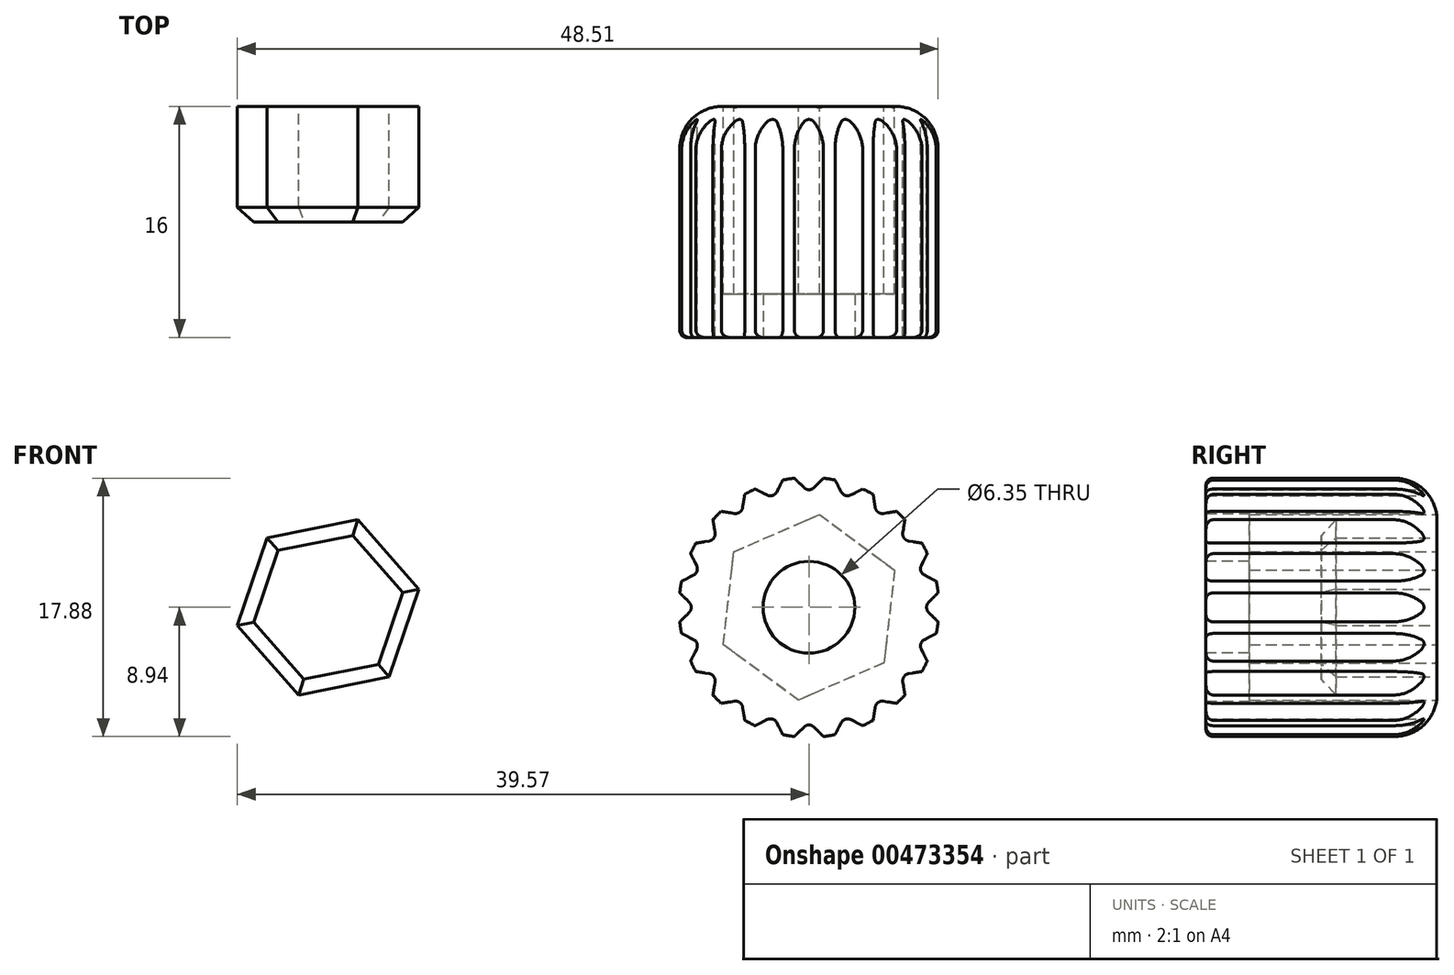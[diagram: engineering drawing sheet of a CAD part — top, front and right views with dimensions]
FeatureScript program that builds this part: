
annotation { "Feature Type Name" : "Feature", "Feature Type Description" : "" }
export const myFeature = defineFeature(function(context is Context, id is Id, definition is map)
    precondition{}
    {
        {
            var Q0;
            Q0=qCreatedBy(makeId("Front.planeOp"),FACE);
            var sketch = newSketch(context, id + "F0", { "sketchPlane" : qUnion([Q0])});
            skCircle(sketch, "E0", {"center": v(0, 0) * mm, "radius": 9 * mm});
            skSolve(sketch);
        }
        {
            var Q0;
            Q0=makeQuery(id+"F0.imprint","IMPRINT",FACE,{"disambiguationData":[TD([[makeQuery(id+"F0.imprint","IMPRINT",EDGE,{"derivedFrom":sQuery(id+"F0.wireOp",EDGE,"E0")}),1.0]])]});
            extrude(context, id + "F1", {"entities" : qUnion([Q0]), "depth" : 16 * mm});
        }
        {
            var Q0;
            Q0=makeQuery(id+"F1.opExtrude","CAP_EDGE",EDGE,{"disambiguationData":[OSD([sQuery(id+"F0.wireOp",EDGE,"E0")])],"isStart":true});
            fillet(context, id + "F2", {"entities" : qUnion([Q0]), "radius" : 3 * mm, "tangentPropagation" : true, "allowEdgeOverflow" : false});
        }
        {
            var Q0;
            Q0=qCreatedBy(makeId("Front.planeOp"),FACE);
            var sketch = newSketch(context, id + "F3", { "sketchPlane" : qUnion([Q0])});
            skLineSegment(sketch, "E1.bottom", {"start": v(10.06, 0) * mm, "end": v(9, 1.06) * mm});
            skLineSegment(sketch, "E1.top", {"start": v(9, -1.06) * mm, "end": v(7.94, 0) * mm});
            skLineSegment(sketch, "E1.left", {"start": v(10.06, 0) * mm, "end": v(9, -1.06) * mm});
            skLineSegment(sketch, "E1.right", {"start": v(9, 1.06) * mm, "end": v(7.94, 0) * mm});
            skPoint(sketch, "E1.middle", {"position": v(9, 0) * mm});
            skSolve(sketch);
        }
        {
            var Q0;
            Q0=makeQuery(id+"F3.imprint","IMPRINT",FACE,{"disambiguationData":[TD([[makeQuery(id+"F3.imprint","IMPRINT",EDGE,{"derivedFrom":sQuery(id+"F3.wireOp",EDGE,"E1.bottom")}),1.0]])]});
            extrude(context, id + "F4", {"entities" : qUnion([Q0]), "depth" : 25 * mm});
        }
        {
            var Q0;
            Q0=makeQuery(id+"F4.opExtrude","SWEPT_BODY",BODY,{"disambiguationData":[OSD([sQuery(id+"F3.wireOp",EDGE,"E1.bottom"),sQuery(id+"F3.wireOp",EDGE,"E1.top"),sQuery(id+"F3.wireOp",EDGE,"E1.left"),sQuery(id+"F3.wireOp",EDGE,"E1.right")])]});
            var Q1;
            Q1=sQuery(id+"F0.wireOp",EDGE,"E0");
            circularPattern(context, id + "F5", {"operationType" : NewBodyOperationType.REMOVE, "entities" : qUnion([Q0]), "axis" : qUnion([Q1]), "angle" : 360 * degree, "instanceCount" : 20, "equalSpace" : true});
        }
        {
            var Q0;
            Q0=qCreatedBy(makeId("Front.planeOp"),FACE);
            var sketch = newSketch(context, id + "F6", { "sketchPlane" : qUnion([Q0])});
            skCircle(sketch, "E2.cCircle", {"center": v(0, 0) * mm, "radius": 6.47 * mm, "construction": true});
            skLineSegment(sketch, "E2.0", {"start": v(5.2, -3.84) * mm, "end": v(-0.73, -6.42) * mm});
            skLineSegment(sketch, "E2.1", {"start": v(-0.73, -6.42) * mm, "end": v(-5.93, -2.58) * mm});
            skLineSegment(sketch, "E2.2", {"start": v(-5.93, -2.58) * mm, "end": v(-5.2, 3.84) * mm});
            skLineSegment(sketch, "E2.3", {"start": v(-5.2, 3.84) * mm, "end": v(0.73, 6.42) * mm});
            skLineSegment(sketch, "E2.4", {"start": v(0.73, 6.42) * mm, "end": v(5.93, 2.58) * mm});
            skLineSegment(sketch, "E2.5", {"start": v(5.93, 2.58) * mm, "end": v(5.2, -3.84) * mm});
            skSolve(sketch);
        }
        {
            var Q0;
            Q0 = qSketchRegion(id + "F6", true);
            extrude(context, id + "F7", {"entities" : qUnion([Q0]), "operationType" : NewBodyOperationType.REMOVE, "depth" : 13 * mm});
        }
        {
            var Q0;
            Q0=qCreatedBy(makeId("Front.planeOp"),FACE);
            var sketch = newSketch(context, id + "F8", { "sketchPlane" : qUnion([Q0])});
            skCircle(sketch, "E3", {"center": v(0, 0) * mm, "radius": 3.17 * mm});
            skSolve(sketch);
        }
        {
            var Q0;
            Q0 = qSketchRegion(id + "F8", true);
            extrude(context, id + "F9", {"entities" : qUnion([Q0]), "operationType" : NewBodyOperationType.REMOVE, "endBound" : BoundingType.SYMMETRIC, "oppositeDirection" : true, "depth" : 40 * mm});
        }
        {
            var Q0;
            Q0=qCreatedBy(makeId("Front.planeOp"),FACE);
            var sketch = newSketch(context, id + "F10", { "sketchPlane" : qUnion([Q0])});
            skCircle(sketch, "E4.cCircle", {"center": v(-33.28, 0) * mm, "radius": 5.55 * mm, "construction": true});
            skLineSegment(sketch, "E4.0", {"start": v(-35.34, -6.07) * mm, "end": v(-39.57, -1.25) * mm});
            skLineSegment(sketch, "E4.1", {"start": v(-39.57, -1.25) * mm, "end": v(-37.5, 4.82) * mm});
            skLineSegment(sketch, "E4.2", {"start": v(-37.5, 4.82) * mm, "end": v(-31.22, 6.07) * mm});
            skLineSegment(sketch, "E4.3", {"start": v(-31.22, 6.07) * mm, "end": v(-27, 1.25) * mm});
            skLineSegment(sketch, "E4.4", {"start": v(-27, 1.25) * mm, "end": v(-29.06, -4.82) * mm});
            skLineSegment(sketch, "E4.5", {"start": v(-29.06, -4.82) * mm, "end": v(-35.34, -6.07) * mm});
            skPoint(sketch, "E4.0.midPoint", {"position": v(-37.45, -3.66) * mm});
            skSolve(sketch);
        }
        {
            var Q0;
            Q0=makeQuery(id+"F10.imprint","IMPRINT",FACE,{"disambiguationData":[TD([[makeQuery(id+"F10.imprint","IMPRINT",EDGE,{"derivedFrom":sQuery(id+"F10.wireOp",EDGE,"E4.0")}),-1.0]])]});
            extrude(context, id + "F11", {"entities" : qUnion([Q0]), "depth" : 8 * mm});
        }
        {
            var Q0;
            Q0=makeQuery(id+"F5.boolean.opBoolean","INTERSECT",EDGE,{"derivedFrom":[makeQuery(id+"F5.opPattern","COPY",FACE,{"derivedFrom":makeQuery(id+"F4.opExtrude","SWEPT_FACE",FACE,{"disambiguationData":[OSD([sQuery(id+"F3.wireOp",EDGE,"E1.right")])]}),"instanceName":"11"}),makeQuery(id+"F5.opPattern","COPY",FACE,{"derivedFrom":makeQuery(id+"F4.opExtrude","SWEPT_FACE",FACE,{"disambiguationData":[OSD([sQuery(id+"F3.wireOp",EDGE,"E1.top")])]}),"instanceName":"12"})]});
            var Q1;
            Q1=makeQuery(id+"F5.boolean.opBoolean","INTERSECT",EDGE,{"derivedFrom":[makeQuery(id+"F5.opPattern","COPY",FACE,{"derivedFrom":makeQuery(id+"F4.opExtrude","SWEPT_FACE",FACE,{"disambiguationData":[OSD([sQuery(id+"F3.wireOp",EDGE,"E1.right")])]}),"instanceName":"10"}),makeQuery(id+"F5.opPattern","COPY",FACE,{"derivedFrom":makeQuery(id+"F4.opExtrude","SWEPT_FACE",FACE,{"disambiguationData":[OSD([sQuery(id+"F3.wireOp",EDGE,"E1.top")])]}),"instanceName":"11"})]});
            var Q2;
            Q2=makeQuery(id+"F5.boolean.opBoolean","INTERSECT",EDGE,{"derivedFrom":[makeQuery(id+"F5.opPattern","COPY",FACE,{"derivedFrom":makeQuery(id+"F4.opExtrude","SWEPT_FACE",FACE,{"disambiguationData":[OSD([sQuery(id+"F3.wireOp",EDGE,"E1.right")])]}),"instanceName":"9"}),makeQuery(id+"F5.opPattern","COPY",FACE,{"derivedFrom":makeQuery(id+"F4.opExtrude","SWEPT_FACE",FACE,{"disambiguationData":[OSD([sQuery(id+"F3.wireOp",EDGE,"E1.top")])]}),"instanceName":"10"})]});
            var Q3;
            Q3=makeQuery(id+"F5.boolean.opBoolean","INTERSECT",EDGE,{"derivedFrom":[makeQuery(id+"F5.opPattern","COPY",FACE,{"derivedFrom":makeQuery(id+"F4.opExtrude","SWEPT_FACE",FACE,{"disambiguationData":[OSD([sQuery(id+"F3.wireOp",EDGE,"E1.right")])]}),"instanceName":"8"}),makeQuery(id+"F5.opPattern","COPY",FACE,{"derivedFrom":makeQuery(id+"F4.opExtrude","SWEPT_FACE",FACE,{"disambiguationData":[OSD([sQuery(id+"F3.wireOp",EDGE,"E1.top")])]}),"instanceName":"9"})]});
            var Q4;
            Q4=makeQuery(id+"F5.boolean.opBoolean","INTERSECT",EDGE,{"derivedFrom":[makeQuery(id+"F5.opPattern","COPY",FACE,{"derivedFrom":makeQuery(id+"F4.opExtrude","SWEPT_FACE",FACE,{"disambiguationData":[OSD([sQuery(id+"F3.wireOp",EDGE,"E1.right")])]}),"instanceName":"7"}),makeQuery(id+"F5.opPattern","COPY",FACE,{"derivedFrom":makeQuery(id+"F4.opExtrude","SWEPT_FACE",FACE,{"disambiguationData":[OSD([sQuery(id+"F3.wireOp",EDGE,"E1.top")])]}),"instanceName":"8"})]});
            var Q5;
            Q5=makeQuery(id+"F5.boolean.opBoolean","INTERSECT",EDGE,{"derivedFrom":[makeQuery(id+"F5.opPattern","COPY",FACE,{"derivedFrom":makeQuery(id+"F4.opExtrude","SWEPT_FACE",FACE,{"disambiguationData":[OSD([sQuery(id+"F3.wireOp",EDGE,"E1.right")])]}),"instanceName":"6"}),makeQuery(id+"F5.opPattern","COPY",FACE,{"derivedFrom":makeQuery(id+"F4.opExtrude","SWEPT_FACE",FACE,{"disambiguationData":[OSD([sQuery(id+"F3.wireOp",EDGE,"E1.top")])]}),"instanceName":"7"})]});
            var Q6;
            Q6=makeQuery(id+"F5.boolean.opBoolean","INTERSECT",EDGE,{"derivedFrom":[makeQuery(id+"F5.opPattern","COPY",FACE,{"derivedFrom":makeQuery(id+"F4.opExtrude","SWEPT_FACE",FACE,{"disambiguationData":[OSD([sQuery(id+"F3.wireOp",EDGE,"E1.right")])]}),"instanceName":"5"}),makeQuery(id+"F5.opPattern","COPY",FACE,{"derivedFrom":makeQuery(id+"F4.opExtrude","SWEPT_FACE",FACE,{"disambiguationData":[OSD([sQuery(id+"F3.wireOp",EDGE,"E1.top")])]}),"instanceName":"6"})]});
            var Q7;
            Q7=makeQuery(id+"F5.boolean.opBoolean","INTERSECT",EDGE,{"derivedFrom":[makeQuery(id+"F5.opPattern","COPY",FACE,{"derivedFrom":makeQuery(id+"F4.opExtrude","SWEPT_FACE",FACE,{"disambiguationData":[OSD([sQuery(id+"F3.wireOp",EDGE,"E1.right")])]}),"instanceName":"4"}),makeQuery(id+"F5.opPattern","COPY",FACE,{"derivedFrom":makeQuery(id+"F4.opExtrude","SWEPT_FACE",FACE,{"disambiguationData":[OSD([sQuery(id+"F3.wireOp",EDGE,"E1.top")])]}),"instanceName":"5"})]});
            var Q8;
            Q8=makeQuery(id+"F5.boolean.opBoolean","INTERSECT",EDGE,{"derivedFrom":[makeQuery(id+"F5.opPattern","COPY",FACE,{"derivedFrom":makeQuery(id+"F4.opExtrude","SWEPT_FACE",FACE,{"disambiguationData":[OSD([sQuery(id+"F3.wireOp",EDGE,"E1.right")])]}),"instanceName":"3"}),makeQuery(id+"F5.opPattern","COPY",FACE,{"derivedFrom":makeQuery(id+"F4.opExtrude","SWEPT_FACE",FACE,{"disambiguationData":[OSD([sQuery(id+"F3.wireOp",EDGE,"E1.top")])]}),"instanceName":"4"})]});
            var Q9;
            Q9=makeQuery(id+"F5.boolean.opBoolean","INTERSECT",EDGE,{"derivedFrom":[makeQuery(id+"F5.opPattern","COPY",FACE,{"derivedFrom":makeQuery(id+"F4.opExtrude","SWEPT_FACE",FACE,{"disambiguationData":[OSD([sQuery(id+"F3.wireOp",EDGE,"E1.right")])]}),"instanceName":"2"}),makeQuery(id+"F5.opPattern","COPY",FACE,{"derivedFrom":makeQuery(id+"F4.opExtrude","SWEPT_FACE",FACE,{"disambiguationData":[OSD([sQuery(id+"F3.wireOp",EDGE,"E1.top")])]}),"instanceName":"3"})]});
            var Q10;
            Q10=makeQuery(id+"F5.boolean.opBoolean","INTERSECT",EDGE,{"derivedFrom":[makeQuery(id+"F5.opPattern","COPY",FACE,{"derivedFrom":makeQuery(id+"F4.opExtrude","SWEPT_FACE",FACE,{"disambiguationData":[OSD([sQuery(id+"F3.wireOp",EDGE,"E1.right")])]}),"instanceName":"1"}),makeQuery(id+"F5.opPattern","COPY",FACE,{"derivedFrom":makeQuery(id+"F4.opExtrude","SWEPT_FACE",FACE,{"disambiguationData":[OSD([sQuery(id+"F3.wireOp",EDGE,"E1.top")])]}),"instanceName":"2"})]});
            var Q11;
            Q11=makeQuery(id+"F5.boolean.opBoolean","INTERSECT",EDGE,{"derivedFrom":[makeQuery(id+"F4.opExtrude","SWEPT_FACE",FACE,{"disambiguationData":[OSD([sQuery(id+"F3.wireOp",EDGE,"E1.right")])]}),makeQuery(id+"F5.opPattern","COPY",FACE,{"derivedFrom":makeQuery(id+"F4.opExtrude","SWEPT_FACE",FACE,{"disambiguationData":[OSD([sQuery(id+"F3.wireOp",EDGE,"E1.top")])]}),"instanceName":"1"})]});
            var Q12;
            Q12=makeQuery(id+"F5.boolean.opBoolean","COPY",EDGE,{"derivedFrom":makeQuery(id+"F5.opPattern","COPY",EDGE,{"derivedFrom":makeQuery(id+"F4.opExtrude","SWEPT_EDGE",EDGE,{"disambiguationData":[OSD([sQuery(id+"F3.wireOp",EDGE,"E1.top"),sQuery(id+"F3.wireOp",EDGE,"E1.right")])]}),"instanceName":"1"})});
            var Q13;
            Q13=makeQuery(id+"F5.boolean.opBoolean","COPY",EDGE,{"derivedFrom":makeQuery(id+"F5.opPattern","COPY",EDGE,{"derivedFrom":makeQuery(id+"F4.opExtrude","SWEPT_EDGE",EDGE,{"disambiguationData":[OSD([sQuery(id+"F3.wireOp",EDGE,"E1.top"),sQuery(id+"F3.wireOp",EDGE,"E1.right")])]}),"instanceName":"2"})});
            var Q14;
            Q14=makeQuery(id+"F5.boolean.opBoolean","COPY",EDGE,{"derivedFrom":makeQuery(id+"F5.opPattern","COPY",EDGE,{"derivedFrom":makeQuery(id+"F4.opExtrude","SWEPT_EDGE",EDGE,{"disambiguationData":[OSD([sQuery(id+"F3.wireOp",EDGE,"E1.top"),sQuery(id+"F3.wireOp",EDGE,"E1.right")])]}),"instanceName":"3"})});
            var Q15;
            Q15=makeQuery(id+"F5.boolean.opBoolean","COPY",EDGE,{"derivedFrom":makeQuery(id+"F5.opPattern","COPY",EDGE,{"derivedFrom":makeQuery(id+"F4.opExtrude","SWEPT_EDGE",EDGE,{"disambiguationData":[OSD([sQuery(id+"F3.wireOp",EDGE,"E1.top"),sQuery(id+"F3.wireOp",EDGE,"E1.right")])]}),"instanceName":"4"})});
            var Q16;
            Q16=makeQuery(id+"F5.boolean.opBoolean","COPY",EDGE,{"derivedFrom":makeQuery(id+"F4.opExtrude","SWEPT_EDGE",EDGE,{"disambiguationData":[OSD([sQuery(id+"F3.wireOp",EDGE,"E1.top"),sQuery(id+"F3.wireOp",EDGE,"E1.right")])]})});
            var Q17;
            Q17=makeQuery(id+"F5.boolean.opBoolean","COPY",EDGE,{"derivedFrom":makeQuery(id+"F5.opPattern","COPY",EDGE,{"derivedFrom":makeQuery(id+"F4.opExtrude","SWEPT_EDGE",EDGE,{"disambiguationData":[OSD([sQuery(id+"F3.wireOp",EDGE,"E1.top"),sQuery(id+"F3.wireOp",EDGE,"E1.right")])]}),"instanceName":"29"})});
            var Q18;
            Q18=makeQuery(id+"F5.boolean.opBoolean","INTERSECT",EDGE,{"derivedFrom":[makeQuery(id+"F4.opExtrude","SWEPT_FACE",FACE,{"disambiguationData":[OSD([sQuery(id+"F3.wireOp",EDGE,"E1.top")])]}),makeQuery(id+"F5.opPattern","COPY",FACE,{"derivedFrom":makeQuery(id+"F4.opExtrude","SWEPT_FACE",FACE,{"disambiguationData":[OSD([sQuery(id+"F3.wireOp",EDGE,"E1.right")])]}),"instanceName":"29"})]});
            var Q19;
            Q19=makeQuery(id+"F5.boolean.opBoolean","INTERSECT",EDGE,{"derivedFrom":[makeQuery(id+"F5.opPattern","COPY",FACE,{"derivedFrom":makeQuery(id+"F4.opExtrude","SWEPT_FACE",FACE,{"disambiguationData":[OSD([sQuery(id+"F3.wireOp",EDGE,"E1.right")])]}),"instanceName":"28"}),makeQuery(id+"F5.opPattern","COPY",FACE,{"derivedFrom":makeQuery(id+"F4.opExtrude","SWEPT_FACE",FACE,{"disambiguationData":[OSD([sQuery(id+"F3.wireOp",EDGE,"E1.top")])]}),"instanceName":"29"})]});
            var Q20;
            Q20=makeQuery(id+"F5.boolean.opBoolean","INTERSECT",EDGE,{"derivedFrom":[makeQuery(id+"F5.opPattern","COPY",FACE,{"derivedFrom":makeQuery(id+"F4.opExtrude","SWEPT_FACE",FACE,{"disambiguationData":[OSD([sQuery(id+"F3.wireOp",EDGE,"E1.right")])]}),"instanceName":"27"}),makeQuery(id+"F5.opPattern","COPY",FACE,{"derivedFrom":makeQuery(id+"F4.opExtrude","SWEPT_FACE",FACE,{"disambiguationData":[OSD([sQuery(id+"F3.wireOp",EDGE,"E1.top")])]}),"instanceName":"28"})]});
            var Q21;
            Q21=makeQuery(id+"F5.boolean.opBoolean","INTERSECT",EDGE,{"derivedFrom":[makeQuery(id+"F5.opPattern","COPY",FACE,{"derivedFrom":makeQuery(id+"F4.opExtrude","SWEPT_FACE",FACE,{"disambiguationData":[OSD([sQuery(id+"F3.wireOp",EDGE,"E1.right")])]}),"instanceName":"26"}),makeQuery(id+"F5.opPattern","COPY",FACE,{"derivedFrom":makeQuery(id+"F4.opExtrude","SWEPT_FACE",FACE,{"disambiguationData":[OSD([sQuery(id+"F3.wireOp",EDGE,"E1.top")])]}),"instanceName":"27"})]});
            var Q22;
            Q22=makeQuery(id+"F5.boolean.opBoolean","COPY",EDGE,{"derivedFrom":makeQuery(id+"F5.opPattern","COPY",EDGE,{"derivedFrom":makeQuery(id+"F4.opExtrude","SWEPT_EDGE",EDGE,{"disambiguationData":[OSD([sQuery(id+"F3.wireOp",EDGE,"E1.top"),sQuery(id+"F3.wireOp",EDGE,"E1.right")])]}),"instanceName":"28"})});
            var Q23;
            Q23=makeQuery(id+"F5.boolean.opBoolean","COPY",EDGE,{"derivedFrom":makeQuery(id+"F5.opPattern","COPY",EDGE,{"derivedFrom":makeQuery(id+"F4.opExtrude","SWEPT_EDGE",EDGE,{"disambiguationData":[OSD([sQuery(id+"F3.wireOp",EDGE,"E1.top"),sQuery(id+"F3.wireOp",EDGE,"E1.right")])]}),"instanceName":"27"})});
            var Q24;
            Q24=makeQuery(id+"F5.boolean.opBoolean","COPY",EDGE,{"derivedFrom":makeQuery(id+"F5.opPattern","COPY",EDGE,{"derivedFrom":makeQuery(id+"F4.opExtrude","SWEPT_EDGE",EDGE,{"disambiguationData":[OSD([sQuery(id+"F3.wireOp",EDGE,"E1.top"),sQuery(id+"F3.wireOp",EDGE,"E1.right")])]}),"instanceName":"26"})});
            var Q25;
            Q25=makeQuery(id+"F5.boolean.opBoolean","INTERSECT",EDGE,{"derivedFrom":[makeQuery(id+"F5.opPattern","COPY",FACE,{"derivedFrom":makeQuery(id+"F4.opExtrude","SWEPT_FACE",FACE,{"disambiguationData":[OSD([sQuery(id+"F3.wireOp",EDGE,"E1.right")])]}),"instanceName":"25"}),makeQuery(id+"F5.opPattern","COPY",FACE,{"derivedFrom":makeQuery(id+"F4.opExtrude","SWEPT_FACE",FACE,{"disambiguationData":[OSD([sQuery(id+"F3.wireOp",EDGE,"E1.top")])]}),"instanceName":"26"})]});
            var Q26;
            Q26=makeQuery(id+"F5.boolean.opBoolean","COPY",EDGE,{"derivedFrom":makeQuery(id+"F5.opPattern","COPY",EDGE,{"derivedFrom":makeQuery(id+"F4.opExtrude","SWEPT_EDGE",EDGE,{"disambiguationData":[OSD([sQuery(id+"F3.wireOp",EDGE,"E1.top"),sQuery(id+"F3.wireOp",EDGE,"E1.right")])]}),"instanceName":"24"})});
            var Q27;
            Q27=makeQuery(id+"F5.boolean.opBoolean","COPY",EDGE,{"derivedFrom":makeQuery(id+"F5.opPattern","COPY",EDGE,{"derivedFrom":makeQuery(id+"F4.opExtrude","SWEPT_EDGE",EDGE,{"disambiguationData":[OSD([sQuery(id+"F3.wireOp",EDGE,"E1.top"),sQuery(id+"F3.wireOp",EDGE,"E1.right")])]}),"instanceName":"25"})});
            var Q28;
            Q28=makeQuery(id+"F5.boolean.opBoolean","INTERSECT",EDGE,{"derivedFrom":[makeQuery(id+"F5.opPattern","COPY",FACE,{"derivedFrom":makeQuery(id+"F4.opExtrude","SWEPT_FACE",FACE,{"disambiguationData":[OSD([sQuery(id+"F3.wireOp",EDGE,"E1.right")])]}),"instanceName":"24"}),makeQuery(id+"F5.opPattern","COPY",FACE,{"derivedFrom":makeQuery(id+"F4.opExtrude","SWEPT_FACE",FACE,{"disambiguationData":[OSD([sQuery(id+"F3.wireOp",EDGE,"E1.top")])]}),"instanceName":"25"})]});
            var Q29;
            Q29=makeQuery(id+"F5.boolean.opBoolean","COPY",EDGE,{"derivedFrom":makeQuery(id+"F5.opPattern","COPY",EDGE,{"derivedFrom":makeQuery(id+"F4.opExtrude","SWEPT_EDGE",EDGE,{"disambiguationData":[OSD([sQuery(id+"F3.wireOp",EDGE,"E1.top"),sQuery(id+"F3.wireOp",EDGE,"E1.right")])]}),"instanceName":"23"})});
            var Q30;
            Q30=makeQuery(id+"F5.boolean.opBoolean","INTERSECT",EDGE,{"derivedFrom":[makeQuery(id+"F5.opPattern","COPY",FACE,{"derivedFrom":makeQuery(id+"F4.opExtrude","SWEPT_FACE",FACE,{"disambiguationData":[OSD([sQuery(id+"F3.wireOp",EDGE,"E1.right")])]}),"instanceName":"23"}),makeQuery(id+"F5.opPattern","COPY",FACE,{"derivedFrom":makeQuery(id+"F4.opExtrude","SWEPT_FACE",FACE,{"disambiguationData":[OSD([sQuery(id+"F3.wireOp",EDGE,"E1.top")])]}),"instanceName":"24"})]});
            var Q31;
            Q31=makeQuery(id+"F5.boolean.opBoolean","INTERSECT",EDGE,{"derivedFrom":[makeQuery(id+"F5.opPattern","COPY",FACE,{"derivedFrom":makeQuery(id+"F4.opExtrude","SWEPT_FACE",FACE,{"disambiguationData":[OSD([sQuery(id+"F3.wireOp",EDGE,"E1.right")])]}),"instanceName":"22"}),makeQuery(id+"F5.opPattern","COPY",FACE,{"derivedFrom":makeQuery(id+"F4.opExtrude","SWEPT_FACE",FACE,{"disambiguationData":[OSD([sQuery(id+"F3.wireOp",EDGE,"E1.top")])]}),"instanceName":"23"})]});
            var Q32;
            Q32=makeQuery(id+"F5.boolean.opBoolean","COPY",EDGE,{"derivedFrom":makeQuery(id+"F5.opPattern","COPY",EDGE,{"derivedFrom":makeQuery(id+"F4.opExtrude","SWEPT_EDGE",EDGE,{"disambiguationData":[OSD([sQuery(id+"F3.wireOp",EDGE,"E1.top"),sQuery(id+"F3.wireOp",EDGE,"E1.right")])]}),"instanceName":"22"})});
            var Q33;
            Q33=makeQuery(id+"F5.boolean.opBoolean","INTERSECT",EDGE,{"derivedFrom":[makeQuery(id+"F5.opPattern","COPY",FACE,{"derivedFrom":makeQuery(id+"F4.opExtrude","SWEPT_FACE",FACE,{"disambiguationData":[OSD([sQuery(id+"F3.wireOp",EDGE,"E1.right")])]}),"instanceName":"21"}),makeQuery(id+"F5.opPattern","COPY",FACE,{"derivedFrom":makeQuery(id+"F4.opExtrude","SWEPT_FACE",FACE,{"disambiguationData":[OSD([sQuery(id+"F3.wireOp",EDGE,"E1.top")])]}),"instanceName":"22"})]});
            var Q34;
            Q34=makeQuery(id+"F5.boolean.opBoolean","COPY",EDGE,{"derivedFrom":makeQuery(id+"F5.opPattern","COPY",EDGE,{"derivedFrom":makeQuery(id+"F4.opExtrude","SWEPT_EDGE",EDGE,{"disambiguationData":[OSD([sQuery(id+"F3.wireOp",EDGE,"E1.top"),sQuery(id+"F3.wireOp",EDGE,"E1.right")])]}),"instanceName":"21"})});
            var Q35;
            Q35=makeQuery(id+"F5.boolean.opBoolean","COPY",EDGE,{"derivedFrom":makeQuery(id+"F5.opPattern","COPY",EDGE,{"derivedFrom":makeQuery(id+"F4.opExtrude","SWEPT_EDGE",EDGE,{"disambiguationData":[OSD([sQuery(id+"F3.wireOp",EDGE,"E1.top"),sQuery(id+"F3.wireOp",EDGE,"E1.right")])]}),"instanceName":"20"})});
            var Q36;
            Q36=makeQuery(id+"F5.boolean.opBoolean","INTERSECT",EDGE,{"derivedFrom":[makeQuery(id+"F5.opPattern","COPY",FACE,{"derivedFrom":makeQuery(id+"F4.opExtrude","SWEPT_FACE",FACE,{"disambiguationData":[OSD([sQuery(id+"F3.wireOp",EDGE,"E1.right")])]}),"instanceName":"20"}),makeQuery(id+"F5.opPattern","COPY",FACE,{"derivedFrom":makeQuery(id+"F4.opExtrude","SWEPT_FACE",FACE,{"disambiguationData":[OSD([sQuery(id+"F3.wireOp",EDGE,"E1.top")])]}),"instanceName":"21"})]});
            var Q37;
            Q37=makeQuery(id+"F5.boolean.opBoolean","INTERSECT",EDGE,{"derivedFrom":[makeQuery(id+"F5.opPattern","COPY",FACE,{"derivedFrom":makeQuery(id+"F4.opExtrude","SWEPT_FACE",FACE,{"disambiguationData":[OSD([sQuery(id+"F3.wireOp",EDGE,"E1.right")])]}),"instanceName":"19"}),makeQuery(id+"F5.opPattern","COPY",FACE,{"derivedFrom":makeQuery(id+"F4.opExtrude","SWEPT_FACE",FACE,{"disambiguationData":[OSD([sQuery(id+"F3.wireOp",EDGE,"E1.top")])]}),"instanceName":"20"})]});
            var Q38;
            Q38=makeQuery(id+"F5.boolean.opBoolean","COPY",EDGE,{"derivedFrom":makeQuery(id+"F5.opPattern","COPY",EDGE,{"derivedFrom":makeQuery(id+"F4.opExtrude","SWEPT_EDGE",EDGE,{"disambiguationData":[OSD([sQuery(id+"F3.wireOp",EDGE,"E1.top"),sQuery(id+"F3.wireOp",EDGE,"E1.right")])]}),"instanceName":"19"})});
            var Q39;
            Q39=makeQuery(id+"F5.boolean.opBoolean","INTERSECT",EDGE,{"derivedFrom":[makeQuery(id+"F5.opPattern","COPY",FACE,{"derivedFrom":makeQuery(id+"F4.opExtrude","SWEPT_FACE",FACE,{"disambiguationData":[OSD([sQuery(id+"F3.wireOp",EDGE,"E1.right")])]}),"instanceName":"18"}),makeQuery(id+"F5.opPattern","COPY",FACE,{"derivedFrom":makeQuery(id+"F4.opExtrude","SWEPT_FACE",FACE,{"disambiguationData":[OSD([sQuery(id+"F3.wireOp",EDGE,"E1.top")])]}),"instanceName":"19"})]});
            var Q40;
            Q40=makeQuery(id+"F5.boolean.opBoolean","COPY",EDGE,{"derivedFrom":makeQuery(id+"F5.opPattern","COPY",EDGE,{"derivedFrom":makeQuery(id+"F4.opExtrude","SWEPT_EDGE",EDGE,{"disambiguationData":[OSD([sQuery(id+"F3.wireOp",EDGE,"E1.top"),sQuery(id+"F3.wireOp",EDGE,"E1.right")])]}),"instanceName":"18"})});
            var Q41;
            Q41=makeQuery(id+"F5.boolean.opBoolean","COPY",EDGE,{"derivedFrom":makeQuery(id+"F5.opPattern","COPY",EDGE,{"derivedFrom":makeQuery(id+"F4.opExtrude","SWEPT_EDGE",EDGE,{"disambiguationData":[OSD([sQuery(id+"F3.wireOp",EDGE,"E1.top"),sQuery(id+"F3.wireOp",EDGE,"E1.right")])]}),"instanceName":"17"})});
            var Q42;
            Q42=makeQuery(id+"F5.boolean.opBoolean","INTERSECT",EDGE,{"derivedFrom":[makeQuery(id+"F5.opPattern","COPY",FACE,{"derivedFrom":makeQuery(id+"F4.opExtrude","SWEPT_FACE",FACE,{"disambiguationData":[OSD([sQuery(id+"F3.wireOp",EDGE,"E1.right")])]}),"instanceName":"17"}),makeQuery(id+"F5.opPattern","COPY",FACE,{"derivedFrom":makeQuery(id+"F4.opExtrude","SWEPT_FACE",FACE,{"disambiguationData":[OSD([sQuery(id+"F3.wireOp",EDGE,"E1.top")])]}),"instanceName":"18"})]});
            var Q43;
            Q43=makeQuery(id+"F5.boolean.opBoolean","INTERSECT",EDGE,{"derivedFrom":[makeQuery(id+"F5.opPattern","COPY",FACE,{"derivedFrom":makeQuery(id+"F4.opExtrude","SWEPT_FACE",FACE,{"disambiguationData":[OSD([sQuery(id+"F3.wireOp",EDGE,"E1.right")])]}),"instanceName":"16"}),makeQuery(id+"F5.opPattern","COPY",FACE,{"derivedFrom":makeQuery(id+"F4.opExtrude","SWEPT_FACE",FACE,{"disambiguationData":[OSD([sQuery(id+"F3.wireOp",EDGE,"E1.top")])]}),"instanceName":"17"})]});
            var Q44;
            Q44=makeQuery(id+"F5.boolean.opBoolean","COPY",EDGE,{"derivedFrom":makeQuery(id+"F5.opPattern","COPY",EDGE,{"derivedFrom":makeQuery(id+"F4.opExtrude","SWEPT_EDGE",EDGE,{"disambiguationData":[OSD([sQuery(id+"F3.wireOp",EDGE,"E1.top"),sQuery(id+"F3.wireOp",EDGE,"E1.right")])]}),"instanceName":"16"})});
            var Q45;
            Q45=makeQuery(id+"F5.boolean.opBoolean","INTERSECT",EDGE,{"derivedFrom":[makeQuery(id+"F5.opPattern","COPY",FACE,{"derivedFrom":makeQuery(id+"F4.opExtrude","SWEPT_FACE",FACE,{"disambiguationData":[OSD([sQuery(id+"F3.wireOp",EDGE,"E1.right")])]}),"instanceName":"15"}),makeQuery(id+"F5.opPattern","COPY",FACE,{"derivedFrom":makeQuery(id+"F4.opExtrude","SWEPT_FACE",FACE,{"disambiguationData":[OSD([sQuery(id+"F3.wireOp",EDGE,"E1.top")])]}),"instanceName":"16"})]});
            var Q46;
            Q46=makeQuery(id+"F5.boolean.opBoolean","COPY",EDGE,{"derivedFrom":makeQuery(id+"F5.opPattern","COPY",EDGE,{"derivedFrom":makeQuery(id+"F4.opExtrude","SWEPT_EDGE",EDGE,{"disambiguationData":[OSD([sQuery(id+"F3.wireOp",EDGE,"E1.top"),sQuery(id+"F3.wireOp",EDGE,"E1.right")])]}),"instanceName":"15"})});
            var Q47;
            Q47=makeQuery(id+"F5.boolean.opBoolean","INTERSECT",EDGE,{"derivedFrom":[makeQuery(id+"F5.opPattern","COPY",FACE,{"derivedFrom":makeQuery(id+"F4.opExtrude","SWEPT_FACE",FACE,{"disambiguationData":[OSD([sQuery(id+"F3.wireOp",EDGE,"E1.right")])]}),"instanceName":"14"}),makeQuery(id+"F5.opPattern","COPY",FACE,{"derivedFrom":makeQuery(id+"F4.opExtrude","SWEPT_FACE",FACE,{"disambiguationData":[OSD([sQuery(id+"F3.wireOp",EDGE,"E1.top")])]}),"instanceName":"15"})]});
            var Q48;
            Q48=makeQuery(id+"F5.boolean.opBoolean","COPY",EDGE,{"derivedFrom":makeQuery(id+"F5.opPattern","COPY",EDGE,{"derivedFrom":makeQuery(id+"F4.opExtrude","SWEPT_EDGE",EDGE,{"disambiguationData":[OSD([sQuery(id+"F3.wireOp",EDGE,"E1.top"),sQuery(id+"F3.wireOp",EDGE,"E1.right")])]}),"instanceName":"14"})});
            var Q49;
            Q49=makeQuery(id+"F5.boolean.opBoolean","INTERSECT",EDGE,{"derivedFrom":[makeQuery(id+"F5.opPattern","COPY",FACE,{"derivedFrom":makeQuery(id+"F4.opExtrude","SWEPT_FACE",FACE,{"disambiguationData":[OSD([sQuery(id+"F3.wireOp",EDGE,"E1.right")])]}),"instanceName":"13"}),makeQuery(id+"F5.opPattern","COPY",FACE,{"derivedFrom":makeQuery(id+"F4.opExtrude","SWEPT_FACE",FACE,{"disambiguationData":[OSD([sQuery(id+"F3.wireOp",EDGE,"E1.top")])]}),"instanceName":"14"})]});
            var Q50;
            Q50=makeQuery(id+"F5.boolean.opBoolean","COPY",EDGE,{"derivedFrom":makeQuery(id+"F5.opPattern","COPY",EDGE,{"derivedFrom":makeQuery(id+"F4.opExtrude","SWEPT_EDGE",EDGE,{"disambiguationData":[OSD([sQuery(id+"F3.wireOp",EDGE,"E1.top"),sQuery(id+"F3.wireOp",EDGE,"E1.right")])]}),"instanceName":"13"})});
            var Q51;
            Q51=makeQuery(id+"F5.boolean.opBoolean","INTERSECT",EDGE,{"derivedFrom":[makeQuery(id+"F5.opPattern","COPY",FACE,{"derivedFrom":makeQuery(id+"F4.opExtrude","SWEPT_FACE",FACE,{"disambiguationData":[OSD([sQuery(id+"F3.wireOp",EDGE,"E1.right")])]}),"instanceName":"12"}),makeQuery(id+"F5.opPattern","COPY",FACE,{"derivedFrom":makeQuery(id+"F4.opExtrude","SWEPT_FACE",FACE,{"disambiguationData":[OSD([sQuery(id+"F3.wireOp",EDGE,"E1.top")])]}),"instanceName":"13"})]});
            var Q52;
            Q52=makeQuery(id+"F5.boolean.opBoolean","COPY",EDGE,{"derivedFrom":makeQuery(id+"F5.opPattern","COPY",EDGE,{"derivedFrom":makeQuery(id+"F4.opExtrude","SWEPT_EDGE",EDGE,{"disambiguationData":[OSD([sQuery(id+"F3.wireOp",EDGE,"E1.top"),sQuery(id+"F3.wireOp",EDGE,"E1.right")])]}),"instanceName":"12"})});
            var Q53;
            Q53=makeQuery(id+"F5.boolean.opBoolean","COPY",EDGE,{"derivedFrom":makeQuery(id+"F5.opPattern","COPY",EDGE,{"derivedFrom":makeQuery(id+"F4.opExtrude","SWEPT_EDGE",EDGE,{"disambiguationData":[OSD([sQuery(id+"F3.wireOp",EDGE,"E1.top"),sQuery(id+"F3.wireOp",EDGE,"E1.right")])]}),"instanceName":"11"})});
            var Q54;
            Q54=makeQuery(id+"F5.boolean.opBoolean","COPY",EDGE,{"derivedFrom":makeQuery(id+"F5.opPattern","COPY",EDGE,{"derivedFrom":makeQuery(id+"F4.opExtrude","SWEPT_EDGE",EDGE,{"disambiguationData":[OSD([sQuery(id+"F3.wireOp",EDGE,"E1.top"),sQuery(id+"F3.wireOp",EDGE,"E1.right")])]}),"instanceName":"10"})});
            var Q55;
            Q55=makeQuery(id+"F5.boolean.opBoolean","COPY",EDGE,{"derivedFrom":makeQuery(id+"F5.opPattern","COPY",EDGE,{"derivedFrom":makeQuery(id+"F4.opExtrude","SWEPT_EDGE",EDGE,{"disambiguationData":[OSD([sQuery(id+"F3.wireOp",EDGE,"E1.top"),sQuery(id+"F3.wireOp",EDGE,"E1.right")])]}),"instanceName":"9"})});
            var Q56;
            Q56=makeQuery(id+"F5.boolean.opBoolean","COPY",EDGE,{"derivedFrom":makeQuery(id+"F5.opPattern","COPY",EDGE,{"derivedFrom":makeQuery(id+"F4.opExtrude","SWEPT_EDGE",EDGE,{"disambiguationData":[OSD([sQuery(id+"F3.wireOp",EDGE,"E1.top"),sQuery(id+"F3.wireOp",EDGE,"E1.right")])]}),"instanceName":"8"})});
            var Q57;
            Q57=makeQuery(id+"F5.boolean.opBoolean","COPY",EDGE,{"derivedFrom":makeQuery(id+"F5.opPattern","COPY",EDGE,{"derivedFrom":makeQuery(id+"F4.opExtrude","SWEPT_EDGE",EDGE,{"disambiguationData":[OSD([sQuery(id+"F3.wireOp",EDGE,"E1.top"),sQuery(id+"F3.wireOp",EDGE,"E1.right")])]}),"instanceName":"7"})});
            var Q58;
            Q58=makeQuery(id+"F5.boolean.opBoolean","COPY",EDGE,{"derivedFrom":makeQuery(id+"F5.opPattern","COPY",EDGE,{"derivedFrom":makeQuery(id+"F4.opExtrude","SWEPT_EDGE",EDGE,{"disambiguationData":[OSD([sQuery(id+"F3.wireOp",EDGE,"E1.top"),sQuery(id+"F3.wireOp",EDGE,"E1.right")])]}),"instanceName":"6"})});
            var Q59;
            Q59=makeQuery(id+"F5.boolean.opBoolean","COPY",EDGE,{"derivedFrom":makeQuery(id+"F5.opPattern","COPY",EDGE,{"derivedFrom":makeQuery(id+"F4.opExtrude","SWEPT_EDGE",EDGE,{"disambiguationData":[OSD([sQuery(id+"F3.wireOp",EDGE,"E1.top"),sQuery(id+"F3.wireOp",EDGE,"E1.right")])]}),"instanceName":"5"})});
            var Q60;
            {var subQ0=sQuery(id+"F0.wireOp",EDGE,"E0");Q60=makeQuery(id+"F5.boolean.opBoolean","SPLIT",EDGE,{"disambiguationData":[TD([makeQuery(id+"F5.opPattern","COPY",FACE,{"derivedFrom":makeQuery(id+"F4.opExtrude","SWEPT_FACE",FACE,{"disambiguationData":[OSD([sQuery(id+"F3.wireOp",EDGE,"E1.right")])]}),"instanceName":"3"})])],"derivedFrom":makeQuery(id+"F1.opExtrude","CAP_EDGE",EDGE,{"disambiguationData":[OSD([subQ0])],"isStart":false})});}
            var Q61;
            {var subQ0=sQuery(id+"F0.wireOp",EDGE,"E0");Q61=makeQuery(id+"F5.boolean.opBoolean","SPLIT",EDGE,{"disambiguationData":[TD([makeQuery(id+"F5.opPattern","COPY",FACE,{"derivedFrom":makeQuery(id+"F4.opExtrude","SWEPT_FACE",FACE,{"disambiguationData":[OSD([sQuery(id+"F3.wireOp",EDGE,"E1.right")])]}),"instanceName":"2"})])],"derivedFrom":makeQuery(id+"F1.opExtrude","CAP_EDGE",EDGE,{"disambiguationData":[OSD([subQ0])],"isStart":false})});}
            var Q62;
            {var subQ0=sQuery(id+"F0.wireOp",EDGE,"E0");Q62=makeQuery(id+"F5.boolean.opBoolean","SPLIT",EDGE,{"disambiguationData":[TD([makeQuery(id+"F5.opPattern","COPY",FACE,{"derivedFrom":makeQuery(id+"F4.opExtrude","SWEPT_FACE",FACE,{"disambiguationData":[OSD([sQuery(id+"F3.wireOp",EDGE,"E1.right")])]}),"instanceName":"4"})])],"derivedFrom":makeQuery(id+"F1.opExtrude","CAP_EDGE",EDGE,{"disambiguationData":[OSD([subQ0])],"isStart":false})});}
            var Q63;
            {var subQ0=sQuery(id+"F0.wireOp",EDGE,"E0");Q63=makeQuery(id+"F5.boolean.opBoolean","SPLIT",EDGE,{"disambiguationData":[TD([makeQuery(id+"F5.opPattern","COPY",FACE,{"derivedFrom":makeQuery(id+"F4.opExtrude","SWEPT_FACE",FACE,{"disambiguationData":[OSD([sQuery(id+"F3.wireOp",EDGE,"E1.right")])]}),"instanceName":"5"})])],"derivedFrom":makeQuery(id+"F1.opExtrude","CAP_EDGE",EDGE,{"disambiguationData":[OSD([subQ0])],"isStart":false})});}
            var Q64;
            {var subQ0=sQuery(id+"F0.wireOp",EDGE,"E0");Q64=makeQuery(id+"F5.boolean.opBoolean","SPLIT",EDGE,{"disambiguationData":[TD([makeQuery(id+"F5.opPattern","COPY",FACE,{"derivedFrom":makeQuery(id+"F4.opExtrude","SWEPT_FACE",FACE,{"disambiguationData":[OSD([sQuery(id+"F3.wireOp",EDGE,"E1.right")])]}),"instanceName":"6"})])],"derivedFrom":makeQuery(id+"F1.opExtrude","CAP_EDGE",EDGE,{"disambiguationData":[OSD([subQ0])],"isStart":false})});}
            var Q65;
            {var subQ0=sQuery(id+"F0.wireOp",EDGE,"E0");Q65=makeQuery(id+"F5.boolean.opBoolean","SPLIT",EDGE,{"disambiguationData":[TD([makeQuery(id+"F5.opPattern","COPY",FACE,{"derivedFrom":makeQuery(id+"F4.opExtrude","SWEPT_FACE",FACE,{"disambiguationData":[OSD([sQuery(id+"F3.wireOp",EDGE,"E1.right")])]}),"instanceName":"7"})])],"derivedFrom":makeQuery(id+"F1.opExtrude","CAP_EDGE",EDGE,{"disambiguationData":[OSD([subQ0])],"isStart":false})});}
            var Q66;
            {var subQ0=sQuery(id+"F0.wireOp",EDGE,"E0");Q66=makeQuery(id+"F5.boolean.opBoolean","SPLIT",EDGE,{"disambiguationData":[TD([makeQuery(id+"F5.opPattern","COPY",FACE,{"derivedFrom":makeQuery(id+"F4.opExtrude","SWEPT_FACE",FACE,{"disambiguationData":[OSD([sQuery(id+"F3.wireOp",EDGE,"E1.right")])]}),"instanceName":"8"})])],"derivedFrom":makeQuery(id+"F1.opExtrude","CAP_EDGE",EDGE,{"disambiguationData":[OSD([subQ0])],"isStart":false})});}
            var Q67;
            {var subQ0=sQuery(id+"F0.wireOp",EDGE,"E0");Q67=makeQuery(id+"F5.boolean.opBoolean","SPLIT",EDGE,{"disambiguationData":[TD([makeQuery(id+"F5.opPattern","COPY",FACE,{"derivedFrom":makeQuery(id+"F4.opExtrude","SWEPT_FACE",FACE,{"disambiguationData":[OSD([sQuery(id+"F3.wireOp",EDGE,"E1.right")])]}),"instanceName":"9"})])],"derivedFrom":makeQuery(id+"F1.opExtrude","CAP_EDGE",EDGE,{"disambiguationData":[OSD([subQ0])],"isStart":false})});}
            var Q68;
            {var subQ0=sQuery(id+"F0.wireOp",EDGE,"E0");Q68=makeQuery(id+"F5.boolean.opBoolean","SPLIT",EDGE,{"disambiguationData":[TD([makeQuery(id+"F5.opPattern","COPY",FACE,{"derivedFrom":makeQuery(id+"F4.opExtrude","SWEPT_FACE",FACE,{"disambiguationData":[OSD([sQuery(id+"F3.wireOp",EDGE,"E1.right")])]}),"instanceName":"10"})])],"derivedFrom":makeQuery(id+"F1.opExtrude","CAP_EDGE",EDGE,{"disambiguationData":[OSD([subQ0])],"isStart":false})});}
            var Q69;
            {var subQ0=sQuery(id+"F0.wireOp",EDGE,"E0");Q69=makeQuery(id+"F5.boolean.opBoolean","SPLIT",EDGE,{"disambiguationData":[TD([makeQuery(id+"F5.opPattern","COPY",FACE,{"derivedFrom":makeQuery(id+"F4.opExtrude","SWEPT_FACE",FACE,{"disambiguationData":[OSD([sQuery(id+"F3.wireOp",EDGE,"E1.right")])]}),"instanceName":"11"})])],"derivedFrom":makeQuery(id+"F1.opExtrude","CAP_EDGE",EDGE,{"disambiguationData":[OSD([subQ0])],"isStart":false})});}
            var Q70;
            {var subQ0=sQuery(id+"F0.wireOp",EDGE,"E0");Q70=makeQuery(id+"F5.boolean.opBoolean","SPLIT",EDGE,{"disambiguationData":[TD([makeQuery(id+"F5.opPattern","COPY",FACE,{"derivedFrom":makeQuery(id+"F4.opExtrude","SWEPT_FACE",FACE,{"disambiguationData":[OSD([sQuery(id+"F3.wireOp",EDGE,"E1.right")])]}),"instanceName":"12"})])],"derivedFrom":makeQuery(id+"F1.opExtrude","CAP_EDGE",EDGE,{"disambiguationData":[OSD([subQ0])],"isStart":false})});}
            var Q71;
            {var subQ0=sQuery(id+"F0.wireOp",EDGE,"E0");Q71=makeQuery(id+"F5.boolean.opBoolean","SPLIT",EDGE,{"disambiguationData":[TD([makeQuery(id+"F5.opPattern","COPY",FACE,{"derivedFrom":makeQuery(id+"F4.opExtrude","SWEPT_FACE",FACE,{"disambiguationData":[OSD([sQuery(id+"F3.wireOp",EDGE,"E1.right")])]}),"instanceName":"13"})])],"derivedFrom":makeQuery(id+"F1.opExtrude","CAP_EDGE",EDGE,{"disambiguationData":[OSD([subQ0])],"isStart":false})});}
            var Q72;
            {var subQ0=sQuery(id+"F0.wireOp",EDGE,"E0");Q72=makeQuery(id+"F5.boolean.opBoolean","SPLIT",EDGE,{"disambiguationData":[TD([makeQuery(id+"F5.opPattern","COPY",FACE,{"derivedFrom":makeQuery(id+"F4.opExtrude","SWEPT_FACE",FACE,{"disambiguationData":[OSD([sQuery(id+"F3.wireOp",EDGE,"E1.right")])]}),"instanceName":"14"})])],"derivedFrom":makeQuery(id+"F1.opExtrude","CAP_EDGE",EDGE,{"disambiguationData":[OSD([subQ0])],"isStart":false})});}
            var Q73;
            {var subQ0=sQuery(id+"F0.wireOp",EDGE,"E0");Q73=makeQuery(id+"F5.boolean.opBoolean","SPLIT",EDGE,{"disambiguationData":[TD([makeQuery(id+"F5.opPattern","COPY",FACE,{"derivedFrom":makeQuery(id+"F4.opExtrude","SWEPT_FACE",FACE,{"disambiguationData":[OSD([sQuery(id+"F3.wireOp",EDGE,"E1.right")])]}),"instanceName":"15"})])],"derivedFrom":makeQuery(id+"F1.opExtrude","CAP_EDGE",EDGE,{"disambiguationData":[OSD([subQ0])],"isStart":false})});}
            var Q74;
            {var subQ0=sQuery(id+"F0.wireOp",EDGE,"E0");Q74=makeQuery(id+"F5.boolean.opBoolean","SPLIT",EDGE,{"disambiguationData":[TD([makeQuery(id+"F5.opPattern","COPY",FACE,{"derivedFrom":makeQuery(id+"F4.opExtrude","SWEPT_FACE",FACE,{"disambiguationData":[OSD([sQuery(id+"F3.wireOp",EDGE,"E1.right")])]}),"instanceName":"16"})])],"derivedFrom":makeQuery(id+"F1.opExtrude","CAP_EDGE",EDGE,{"disambiguationData":[OSD([subQ0])],"isStart":false})});}
            var Q75;
            {var subQ0=sQuery(id+"F0.wireOp",EDGE,"E0");Q75=makeQuery(id+"F5.boolean.opBoolean","SPLIT",EDGE,{"disambiguationData":[TD([makeQuery(id+"F5.opPattern","COPY",FACE,{"derivedFrom":makeQuery(id+"F4.opExtrude","SWEPT_FACE",FACE,{"disambiguationData":[OSD([sQuery(id+"F3.wireOp",EDGE,"E1.right")])]}),"instanceName":"17"})])],"derivedFrom":makeQuery(id+"F1.opExtrude","CAP_EDGE",EDGE,{"disambiguationData":[OSD([subQ0])],"isStart":false})});}
            var Q76;
            {var subQ0=sQuery(id+"F0.wireOp",EDGE,"E0");Q76=makeQuery(id+"F5.boolean.opBoolean","SPLIT",EDGE,{"disambiguationData":[TD([makeQuery(id+"F5.opPattern","COPY",FACE,{"derivedFrom":makeQuery(id+"F4.opExtrude","SWEPT_FACE",FACE,{"disambiguationData":[OSD([sQuery(id+"F3.wireOp",EDGE,"E1.right")])]}),"instanceName":"18"})])],"derivedFrom":makeQuery(id+"F1.opExtrude","CAP_EDGE",EDGE,{"disambiguationData":[OSD([subQ0])],"isStart":false})});}
            var Q77;
            {var subQ0=sQuery(id+"F0.wireOp",EDGE,"E0");Q77=makeQuery(id+"F5.boolean.opBoolean","SPLIT",EDGE,{"disambiguationData":[TD([makeQuery(id+"F4.opExtrude","SWEPT_FACE",FACE,{"disambiguationData":[OSD([sQuery(id+"F3.wireOp",EDGE,"E1.top")])]})])],"derivedFrom":makeQuery(id+"F1.opExtrude","CAP_EDGE",EDGE,{"disambiguationData":[OSD([subQ0])],"isStart":false})});}
            var Q78;
            {var subQ0=sQuery(id+"F0.wireOp",EDGE,"E0");Q78=makeQuery(id+"F5.boolean.opBoolean","SPLIT",EDGE,{"disambiguationData":[TD([makeQuery(id+"F4.opExtrude","SWEPT_FACE",FACE,{"disambiguationData":[OSD([sQuery(id+"F3.wireOp",EDGE,"E1.right")])]})])],"derivedFrom":makeQuery(id+"F1.opExtrude","CAP_EDGE",EDGE,{"disambiguationData":[OSD([subQ0])],"isStart":false})});}
            var Q79;
            {var subQ0=sQuery(id+"F0.wireOp",EDGE,"E0");Q79=makeQuery(id+"F5.boolean.opBoolean","SPLIT",EDGE,{"disambiguationData":[TD([makeQuery(id+"F5.opPattern","COPY",FACE,{"derivedFrom":makeQuery(id+"F4.opExtrude","SWEPT_FACE",FACE,{"disambiguationData":[OSD([sQuery(id+"F3.wireOp",EDGE,"E1.right")])]}),"instanceName":"1"})])],"derivedFrom":makeQuery(id+"F1.opExtrude","CAP_EDGE",EDGE,{"disambiguationData":[OSD([subQ0])],"isStart":false})});}
            fillet(context, id + "F12", {"entities" : qUnion([Q0, Q1, Q2, Q3, Q4, Q5, Q6, Q7, Q8, Q9, Q10, Q11, Q12, Q13, Q14, Q15, Q16, Q17, Q18, Q19, Q20, Q21, Q22, Q23, Q24, Q25, Q26, Q27, Q28, Q29, Q30, Q31, Q32, Q33, Q34, Q35, Q36, Q37, Q38, Q39, Q40, Q41, Q42, Q43, Q44, Q45, Q46, Q47, Q48, Q49, Q50, Q51, Q52, Q53, Q54, Q55, Q56, Q57, Q58, Q59, Q60, Q61, Q62, Q63, Q64, Q65, Q66, Q67, Q68, Q69, Q70, Q71, Q72, Q73, Q74, Q75, Q76, Q77, Q78, Q79]), "radius" : .5 * mm, "tangentPropagation" : true, "allowEdgeOverflow" : false});
        }
        {
            var Q0;
            Q0=makeQuery(id+"F11.opExtrude","CAP_EDGE",EDGE,{"disambiguationData":[OSD([sQuery(id+"F10.wireOp",EDGE,"E4.3")])],"isStart":false});
            var Q1;
            Q1=makeQuery(id+"F11.opExtrude","CAP_EDGE",EDGE,{"disambiguationData":[OSD([sQuery(id+"F10.wireOp",EDGE,"E4.2")])],"isStart":false});
            var Q2;
            Q2=makeQuery(id+"F11.opExtrude","CAP_EDGE",EDGE,{"disambiguationData":[OSD([sQuery(id+"F10.wireOp",EDGE,"E4.1")])],"isStart":false});
            var Q3;
            Q3=makeQuery(id+"F11.opExtrude","CAP_EDGE",EDGE,{"disambiguationData":[OSD([sQuery(id+"F10.wireOp",EDGE,"E4.0")])],"isStart":false});
            var Q4;
            Q4=makeQuery(id+"F11.opExtrude","CAP_EDGE",EDGE,{"disambiguationData":[OSD([sQuery(id+"F10.wireOp",EDGE,"E4.5")])],"isStart":false});
            var Q5;
            Q5=makeQuery(id+"F11.opExtrude","CAP_EDGE",EDGE,{"disambiguationData":[OSD([sQuery(id+"F10.wireOp",EDGE,"E4.4")])],"isStart":false});
            chamfer(context, id + "F13", {"entities" : qUnion([Q0, Q1, Q2, Q3, Q4, Q5]), "width" : 1 * mm, "tangentPropagation" : true});
        }
    });
